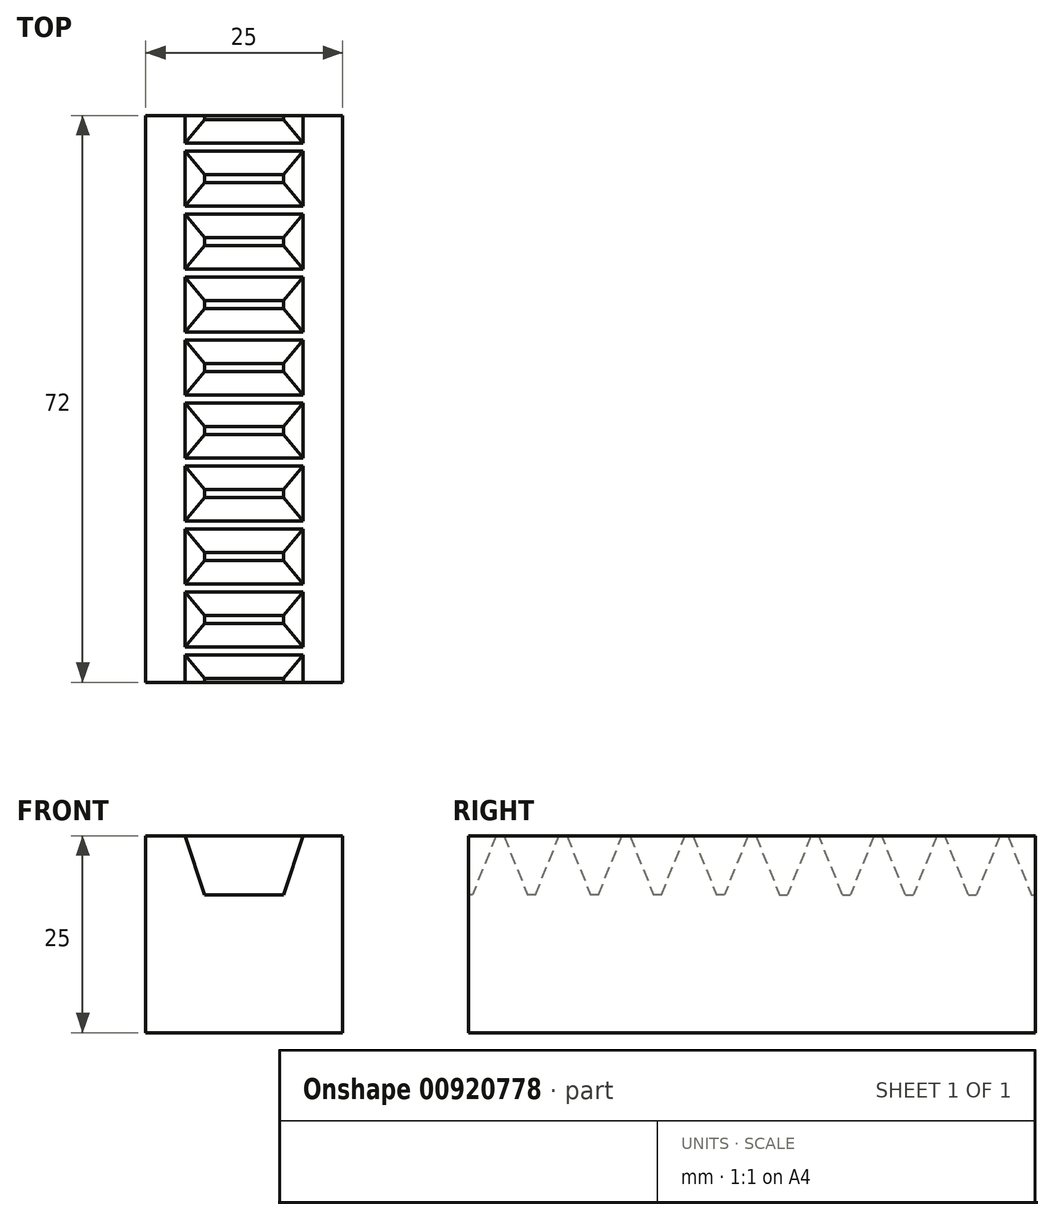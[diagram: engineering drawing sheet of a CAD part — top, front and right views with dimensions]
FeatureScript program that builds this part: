
annotation { "Feature Type Name" : "Feature", "Feature Type Description" : "" }
export const myFeature = defineFeature(function(context is Context, id is Id, definition is map)
    precondition{}
    {
        {
            var Q0;
            Q0=qCreatedBy(makeId("Front.planeOp"),FACE);
            var sketch = newSketch(context, id + "F0", { "sketchPlane" : qUnion([Q0])});
            skLineSegment(sketch, "E0", {"start": v(0, 0) * mm, "end": v(0, -12.5) * mm});
            skLineSegment(sketch, "E1", {"start": v(0, -12.5) * mm, "end": v(-12.5, -12.5) * mm});
            skLineSegment(sketch, "E2", {"start": v(-12.5, -12.5) * mm, "end": v(-12.5, 12.5) * mm});
            skLineSegment(sketch, "E3", {"start": v(-12.5, 12.5) * mm, "end": v(-7.5, 12.5) * mm});
            skLineSegment(sketch, "E4", {"start": v(-7.5, 12.5) * mm, "end": v(-5, 5) * mm});
            skLineSegment(sketch, "E5", {"start": v(-5, 5) * mm, "end": v(0, 5) * mm});
            skLineSegment(sketch, "E6", {"start": v(0, 5) * mm, "end": v(0, 0) * mm});
            skSolve(sketch);
        }
        {
            var Q0;
            Q0 = qSketchRegion(id + "F0", true);
            extrude(context, id + "F1", {"entities" : qUnion([Q0]), "depth" : 36 * mm, "offsetDistance" : 25 * mm});
        }
        {
            var Q0;
            Q0=makeQuery(id+"F1.opExtrude","SWEPT_FACE",FACE,{"disambiguationData":[OSD([sQuery(id+"F0.wireOp",EDGE,"E0"),sQuery(id+"F0.wireOp",EDGE,"E6")])]});
            var sketch = newSketch(context, id + "F2", { "sketchPlane" : qUnion([Q0])});
            skLineSegment(sketch, "E7", {"start": v(-36, 5) * mm, "end": v(-36, 2.38) * mm});
            skLineSegment(sketch, "E8", {"start": v(-36, 2.38) * mm, "end": v(0, 2.38) * mm});
            skLineSegment(sketch, "E9", {"start": v(0, 2.38) * mm, "end": v(0, 5) * mm});
            skLineSegment(sketch, "E10", {"start": v(-3.5, 12.5) * mm, "end": v(-4.5, 12.5) * mm});
            skLineSegment(sketch, "E11", {"start": v(-4.5, 12.5) * mm, "end": v(-7.5, 5) * mm});
            skLineSegment(sketch, "E12", {"start": v(-7.5, 5) * mm, "end": v(-8.5, 5) * mm});
            skLineSegment(sketch, "E13", {"start": v(-8.5, 5) * mm, "end": v(-11.5, 12.5) * mm});
            skLineSegment(sketch, "E14", {"start": v(-11.5, 12.5) * mm, "end": v(-12.5, 12.5) * mm});
            skLineSegment(sketch, "E15", {"start": v(-12.5, 12.5) * mm, "end": v(-15.5, 5) * mm});
            skLineSegment(sketch, "E16", {"start": v(-15.5, 5) * mm, "end": v(-16.5, 5) * mm});
            skLineSegment(sketch, "E17", {"start": v(-16.5, 5) * mm, "end": v(-19.5, 12.5) * mm});
            skLineSegment(sketch, "E18", {"start": v(-19.5, 12.5) * mm, "end": v(-20.5, 12.5) * mm});
            skLineSegment(sketch, "E19", {"start": v(-20.5, 12.5) * mm, "end": v(-23.5, 5) * mm});
            skLineSegment(sketch, "E20", {"start": v(-23.5, 5) * mm, "end": v(-24.5, 5) * mm});
            skLineSegment(sketch, "E21", {"start": v(-24.5, 5) * mm, "end": v(-27.5, 12.5) * mm});
            skLineSegment(sketch, "E22", {"start": v(-27.5, 12.5) * mm, "end": v(-28.5, 12.5) * mm});
            skLineSegment(sketch, "E23", {"start": v(-28.5, 12.5) * mm, "end": v(-31.5, 5) * mm});
            skLineSegment(sketch, "E24", {"start": v(-31.5, 5) * mm, "end": v(-32.5, 5) * mm});
            skLineSegment(sketch, "E25", {"start": v(-36, 12.5) * mm, "end": v(-36, 5) * mm});
            skLineSegment(sketch, "E26", {"start": v(-36, 12.5) * mm, "end": v(-35.5, 12.5) * mm});
            skLineSegment(sketch, "E27", {"start": v(-35.5, 12.5) * mm, "end": v(-32.5, 5) * mm});
            skLineSegment(sketch, "E28", {"start": v(-3.5, 12.5) * mm, "end": v(-0.5, 5) * mm});
            skLineSegment(sketch, "E29", {"start": v(-0.5, 5) * mm, "end": v(0, 5) * mm});
            skSolve(sketch);
        }
        {
            var Q0;
            Q0 = qSketchRegion(id + "F2", true);
            extrude(context, id + "F3", {"entities" : qUnion([Q0]), "operationType" : NewBodyOperationType.ADD, "oppositeDirection" : true, "depth" : 10.4 * mm, "offsetDistance" : 25 * mm});
        }
        {
            var Q0;
            Q0=makeQuery(id+"F1.opExtrude","SWEPT_BODY",BODY,{"disambiguationData":[OSD([sQuery(id+"F0.wireOp",EDGE,"E0"),sQuery(id+"F0.wireOp",EDGE,"E1"),sQuery(id+"F0.wireOp",EDGE,"E2"),sQuery(id+"F0.wireOp",EDGE,"E3"),sQuery(id+"F0.wireOp",EDGE,"E4"),sQuery(id+"F0.wireOp",EDGE,"E5"),sQuery(id+"F0.wireOp",EDGE,"E6")])]});
            var Q1;
            Q1=qCreatedBy(makeId("Right.planeOp"),FACE);
            mirror(context, id + "F4", {"operationType" : NewBodyOperationType.ADD, "entities" : qUnion([Q0]), "mirrorPlane" : qUnion([Q1])});
        }
        {
            var Q0;
            {var subQ0=makeQuery(id+"F3.boolean.opBoolean","MERGE",FACE,{"derivedFrom":[makeQuery(id+"F1.opExtrude","CAP_FACE",FACE,{"disambiguationData":[OSD([sQuery(id+"F0.wireOp",EDGE,"E0"),sQuery(id+"F0.wireOp",EDGE,"E1"),sQuery(id+"F0.wireOp",EDGE,"E2"),sQuery(id+"F0.wireOp",EDGE,"E3"),sQuery(id+"F0.wireOp",EDGE,"E4"),sQuery(id+"F0.wireOp",EDGE,"E5"),sQuery(id+"F0.wireOp",EDGE,"E6")])],"isStart":false}),makeQuery(id+"F3.opExtrude","SWEPT_FACE",FACE,{"disambiguationData":[OSD([sQuery(id+"F2.wireOp",EDGE,"E7"),sQuery(id+"F2.wireOp",EDGE,"E25")])]})]});Q0=makeQuery(id+"F4.boolean.opBoolean","MERGE",FACE,{"derivedFrom":[subQ0,makeQuery(id+"F4.opPattern","COPY",FACE,{"derivedFrom":subQ0,"instanceName":"1"})]});}
            cPlane(context, id + "F5", {"entities" : qUnion([Q0]), "cplaneType" : CPlaneType.OFFSET, "offset" : 0 * mm, "width" : 150 * mm, "height" : 150 * mm});
        }
        {
            var Q0;
            Q0=makeQuery(id+"F1.opExtrude","SWEPT_BODY",BODY,{"disambiguationData":[OSD([sQuery(id+"F0.wireOp",EDGE,"E0"),sQuery(id+"F0.wireOp",EDGE,"E1"),sQuery(id+"F0.wireOp",EDGE,"E2"),sQuery(id+"F0.wireOp",EDGE,"E3"),sQuery(id+"F0.wireOp",EDGE,"E4"),sQuery(id+"F0.wireOp",EDGE,"E5"),sQuery(id+"F0.wireOp",EDGE,"E6")])]});
            var Q1;
            Q1=qCreatedBy(id+"F5.planeOp",FACE);
            mirror(context, id + "F6", {"operationType" : NewBodyOperationType.ADD, "entities" : qUnion([Q0]), "mirrorPlane" : qUnion([Q1])});
        }
    });
